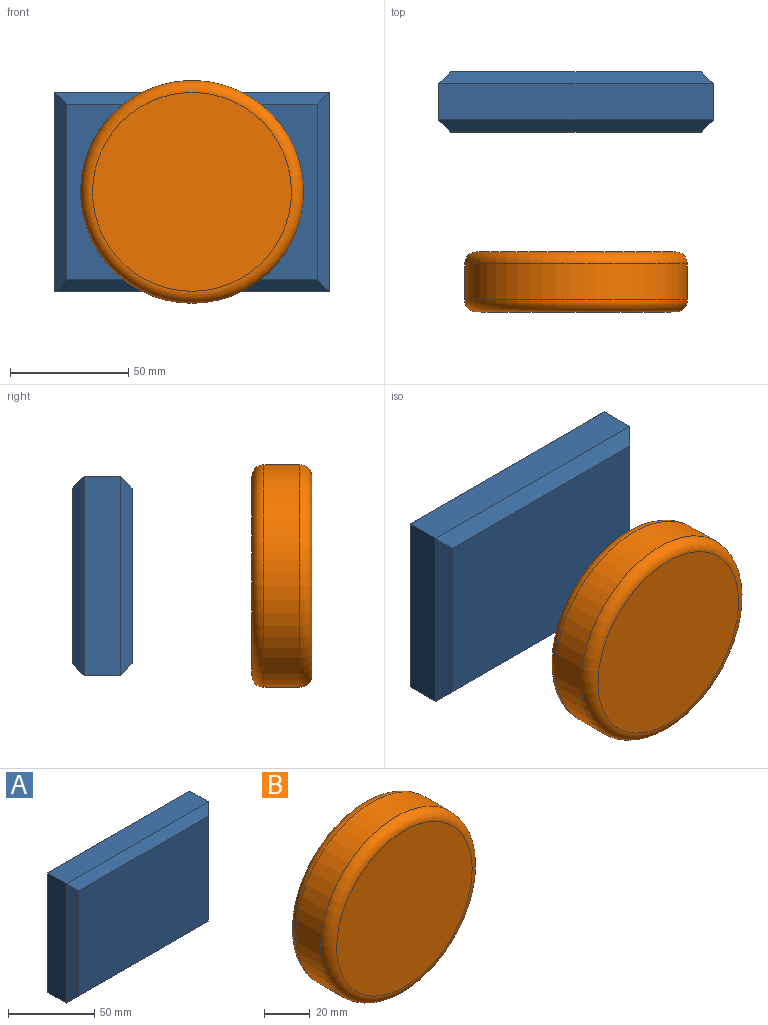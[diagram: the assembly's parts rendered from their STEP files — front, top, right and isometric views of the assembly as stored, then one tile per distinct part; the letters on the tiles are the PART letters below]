
ASSEMBLY  parts=2 mates=1
PART A: 14 faces, bbox 116.3x25.4x84.5 mm
  f0: plane 116.26x15.24mm, normal (0,0,1), area 1771.7mm2, adj f1,f3,f7,f11
  f1: plane 84.54x15.24mm, normal (-1,0,0), area 1288.3mm2, adj f0,f2,f6,f10
  f2: plane 116.26x15.24mm, normal (0,0,-1), area 1771.7mm2, adj f1,f3,f8,f12
  f3: plane 84.54x15.24mm, normal (1,0,0), area 1288.3mm2, adj f0,f2,f9,f13
  f4: plane 106.1x74.38mm, normal (0,-1,0), area 7890.8mm2, adj f10,f11,f12,f13
  f5: plane 106.1x74.38mm, normal (0,1,0), area 7890.8mm2, adj f6,f7,f8,f9
  f6: plane 84.54x5.08mm, normal (-0.71,0.71,0), area 570.8mm2, adj f1,f5,f7,f8
  f7: plane 116.26x5.08mm, normal (0,0.71,0.71), area 798.7mm2, adj f0,f5,f6,f9
  f8: plane 116.26x5.08mm, normal (0,0.71,-0.71), area 798.7mm2, adj f2,f5,f6,f9
  f9: plane 84.54x5.08mm, normal (0.71,0.71,0), area 570.8mm2, adj f3,f5,f7,f8
  f10: plane 84.54x5.08mm, normal (-0.71,-0.71,0), area 570.8mm2, adj f1,f4,f11,f12
  f11: plane 116.26x5.08mm, normal (0,-0.71,0.71), area 798.7mm2, adj f0,f4,f10,f13
  f12: plane 116.26x5.08mm, normal (0,-0.71,-0.71), area 798.7mm2, adj f2,f4,f10,f13
  f13: plane 84.54x5.08mm, normal (0.71,-0.71,0), area 570.8mm2, adj f3,f4,f11,f12
PART B: 5 faces, bbox 102.1x25.4x102.1 mm
  f0: cylinder r=47.18mm len=94.35mm, axis (0,1,0), area 4517.4mm2, adj f3,f4
  f1: plane 84.19x84.19mm, normal (0,-1,0), area 5567.3mm2, adj f4
  f2: plane 84.19x84.19mm, normal (0,1,0), area 5567.3mm2, adj f3
  f3: torus R=42.1mm, axis (0,-1,0), area 2272.8mm2, adj f0,f2
  f4: torus R=42.1mm, axis (0,-1,0), area 2272.8mm2, adj f0,f1
PLACE A t=(123.11,24.44,21.18)mm
PLACE B t=(42.17,-51.76,6.09)mm
MATE fastened A.f4 <-> B.f0  axis (0,-1,0) through (53.39,-0.96,16.14)mm
